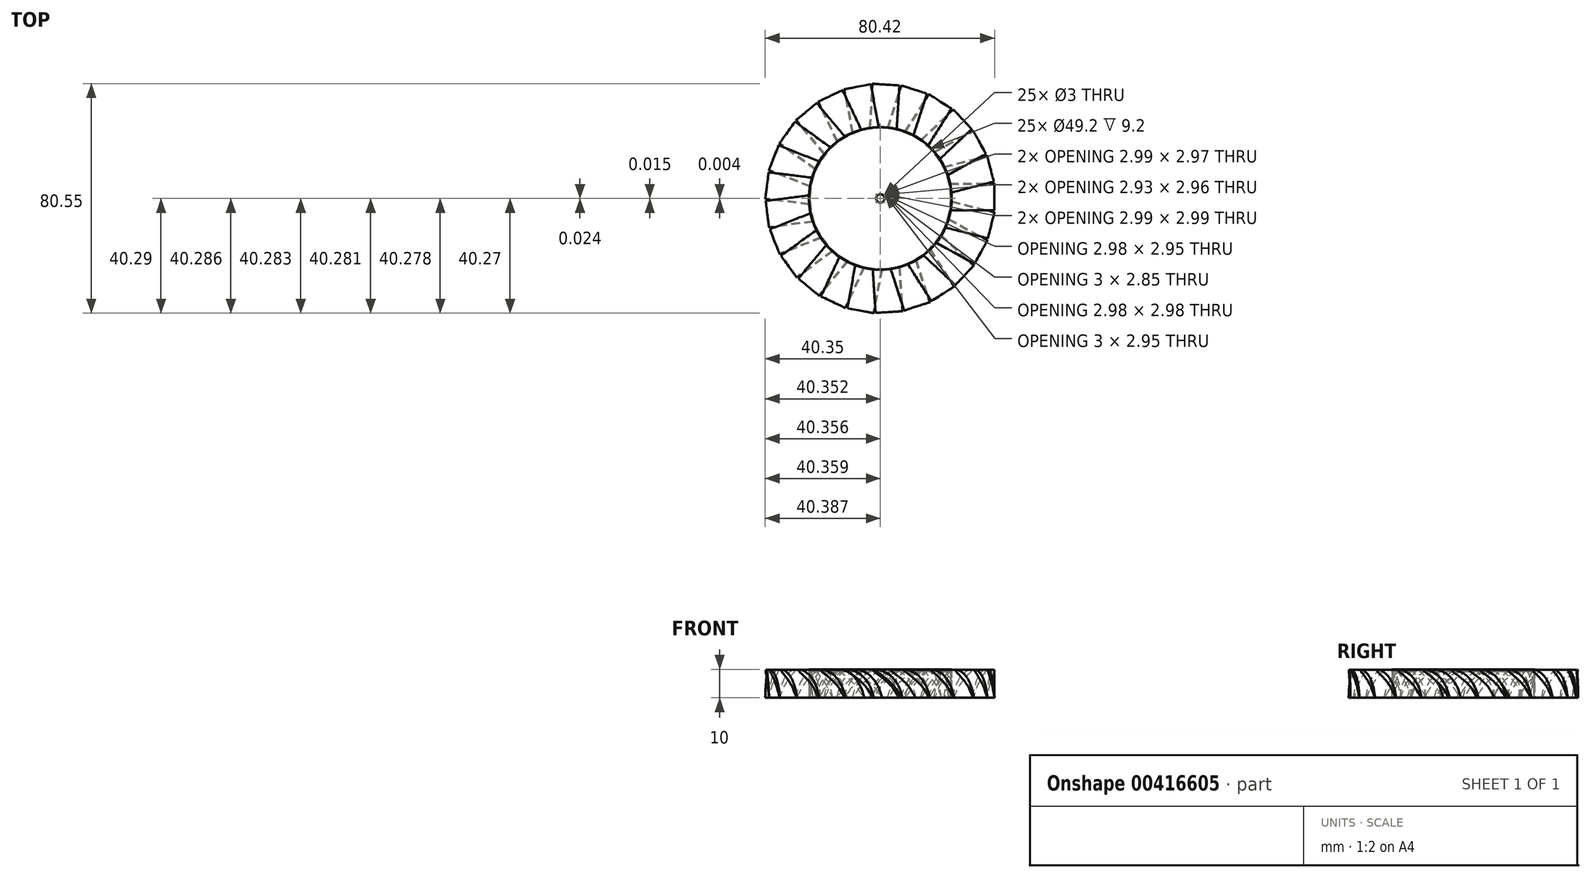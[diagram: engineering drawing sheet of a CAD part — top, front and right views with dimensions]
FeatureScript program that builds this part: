
annotation { "Feature Type Name" : "Feature", "Feature Type Description" : "" }
export const myFeature = defineFeature(function(context is Context, id is Id, definition is map)
    precondition{}
    {
        {
            var Q0;
            Q0=qCreatedBy(makeId("Top.planeOp"),FACE);
            var sketch = newSketch(context, id + "F0", { "sketchPlane" : qUnion([Q0])});
            skCircle(sketch, "E0", {"center": v(0, 0) * mm, "radius": 25 * mm});
            skCircle(sketch, "E1", {"center": v(0, 0) * mm, "radius": 1.5 * mm});
            skSolve(sketch);
        }
        {
            var Q0;
            Q0 = qSketchRegion(id + "F0", true);
            extrude(context, id + "F1", {"entities" : qUnion([Q0]), "depth" : 10 * mm});
        }
        {
            var Q0;
            Q0=qCreatedBy(makeId("Right.planeOp"),FACE);
            cPlane(context, id + "F2", {"entities" : qUnion([Q0]), "cplaneType" : CPlaneType.OFFSET, "offset" : 40 * mm, "width" : 150 * mm, "height" : 150 * mm});
        }
        {
            var Q0;
            Q0=qCreatedBy(id+"F2.planeOp",FACE);
            var sketch = newSketch(context, id + "F3", { "sketchPlane" : qUnion([Q0])});
            skLineSegment(sketch, "E2", {"start": v(4.94, 0) * mm, "end": v(5.34, 0) * mm});
            skFitSpline(sketch, "E3", {"points": [v(5.34, 0) * mm, v(3.8, 4.27) * mm, v(0, 8.6) * mm, v(-4.2, 9.74) * mm, v(-1.78, 7.72) * mm, v(1.72, 4.7) * mm, v(4.94, 0) * mm], "startDerivative": vector(-19.2, 60.77) * mm, "endDerivative": vector(27.5, -47.99) * mm});
            skSolve(sketch);
        }
        {
            var Q0;
            Q0 = qSketchRegion(id + "F3", true);
            extrude(context, id + "F4", {"entities" : qUnion([Q0]), "operationType" : NewBodyOperationType.ADD, "endBound" : BoundingType.UP_TO_NEXT, "oppositeDirection" : true, "depth" : 20 * mm});
        }
        {
            var Q0;
            Q0=makeQuery(id+"F1.opExtrude","SWEPT_BODY",BODY,{"disambiguationData":[OSD([sQuery(id+"F0.wireOp",EDGE,"E0"),sQuery(id+"F0.wireOp",EDGE,"E1")])]});
            var Q1;
            Q1=makeQuery(id+"F1.opExtrude","SWEPT_FACE",FACE,{"disambiguationData":[OSD([sQuery(id+"F0.wireOp",EDGE,"E0")])]});
            circularPattern(context, id + "F5", {"entities" : qUnion([Q0]), "axis" : qUnion([Q1]), "angle" : 360 * degree, "instanceCount" : 25, "equalSpace" : true});
        }
        {
            var Q0;
            Q0=makeQuery(id+"F4.boolean.opBoolean","MERGE",FACE,{"derivedFrom":[makeQuery(id+"F1.opExtrude","CAP_FACE",FACE,{"disambiguationData":[OSD([sQuery(id+"F0.wireOp",EDGE,"E0"),sQuery(id+"F0.wireOp",EDGE,"E1")])],"isStart":true}),makeQuery(id+"F4.opExtrude","SWEPT_FACE",FACE,{"disambiguationData":[OSD([sQuery(id+"F3.wireOp",EDGE,"E2")])]})]});
            var sketch = newSketch(context, id + "F6", { "sketchPlane" : qUnion([Q0])});
            skCircle(sketch, "E4", {"center": v(0, 0) * mm, "radius": 24.6 * mm});
            skSolve(sketch);
        }
        {
            var Q0;
            Q0=makeQuery(id+"F6.imprint","IMPRINT",FACE,{"disambiguationData":[TD([[makeQuery(id+"F6.imprint","IMPRINT",EDGE,{"derivedFrom":sQuery(id+"F6.wireOp",EDGE,"E4")}),1.0]])]});
            extrude(context, id + "F7", {"entities" : qUnion([Q0]), "operationType" : NewBodyOperationType.REMOVE, "oppositeDirection" : true, "depth" : 9.2 * mm});
        }
    });
